# Revit family: Electronics_Masking-Loudspeakers_Biamp_Cambridge_Low-Profile-Loudspeakers_DS1390_1398
name_source: partatom
category: Communication Devices
units: mm (PartAtom-declared; Revit-internal decimal feet)

## family parameters
Cut with Voids When Loaded = No
Host = Face
Maintain Annotation Orientation = No
OmniClass Number = 23.85.10.11.11
OmniClass Title = Sound and Signal Devices
Part Type = Normal
Room Calculation Point = No
Round Connector Dimension = Use Diameter
Shared = No

## types (4) — shared parameters
Cabling = 2 Conductor 18AWG to 16AWG, plenum rated
Connections = 2- Wire Pigtail
Cooling = Front vented
Default Elevation = 48 "
Depth = 5.25 "
Driver Diameter = 4 inches × 1.5 inches (102 mm × 38 mm)
Frequency Response = -10dB down: 160Hz to 6300Hz
Height = 1.8 "
Loudspeaker Type = Dual horizontally opposed high performance drivers. 70.7 V
Manufacturer = Biamp
Nominal Dispersion = 160° H x 325° V
Nominal Impedance = 4 ohm
Product Documentation Link = https://downloads.biamp.com
Product Page URL = https://www.biamp.com
Product data url = https://www.bimobject.com
Sensitivity = 2.83 V at 1 m: 80.7dB SPL
Shipping Dimensions = 12.80” x 10.82” x 14.29” (10-pack)
URL = https://www.biamp.com
Width = 6.25 "

## per-type parameters (varying)
| type | Certifications | Compliance | DS1390 | DS1398 | Description | Housing Material | Model | Output Power Rating | Power Handling | Quantity Drivers | Shipping Weight | Transformer Taps | Weight |
| DS1390 White | UL1480 and CSA C22.2 60065 | - | Yes | No | Dynasound® DS1390 Low Profile Sound Masking and Paging Speaker | Biamp - Metal - White | DS1390 | - | 4 Watts at 70.7 V | - | 15.85 lbf | 1/8,1/4, 1/2,1,2,4 watts | 2.00 lbf |
| DS1398 White | - | ETL Listed (USA), CSA Listed (Canada) | No | Yes | Dynasound® DS1398 Low Profile Sound Masking and Paging Speaker | Biamp - Metal - White | DS1398 | 10W continuous | - | 2 | 20.80 lbf | - | 1.75 lbf |
| DS1390 Black | UL1480 and CSA C22.2 60065 | - | Yes | No | Dynasound® DS1390 Low Profile Sound Masking and Paging Speaker | Biamp - Metal - Black | DS1390 | - | 4 Watts at 70.7 V | - | 15.85 lbf | 1/8,1/4, 1/2,1,2,4 watts | 2.00 lbf |
| DS1398 Black | - | ETL Listed (USA), CSA Listed (Canada) | No | Yes | Dynasound® DS1398 Low Profile Sound Masking and Paging Speaker | Biamp - Metal - Black | DS1398 | 10W continuous | - | 2 | 20.80 lbf | - | 1.75 lbf |

## geometry (parser evidence)
native form markers: Sweep x2
no freeform markers — native parametric forms only
